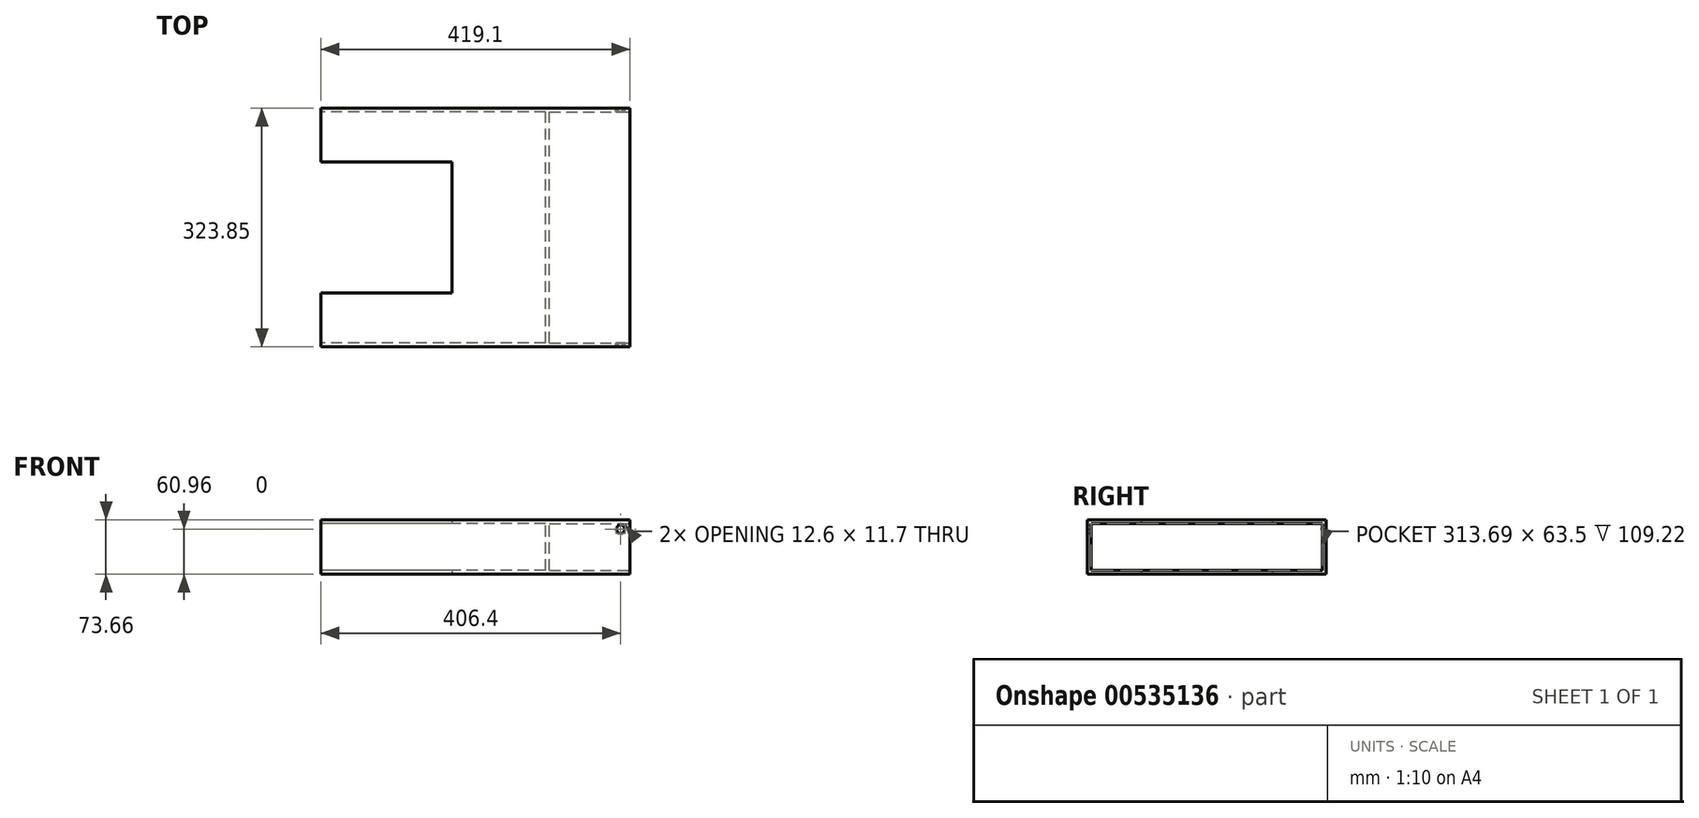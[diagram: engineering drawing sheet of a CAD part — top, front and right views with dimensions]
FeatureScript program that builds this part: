
annotation { "Feature Type Name" : "Feature", "Feature Type Description" : "" }
export const myFeature = defineFeature(function(context is Context, id is Id, definition is map)
    precondition{}
    {
        {
            var Q0;
            Q0=qCreatedBy(makeId("Front.planeOp"),FACE);
            var sketch = newSketch(context, id + "F0", { "sketchPlane" : qUnion([Q0])});
            skLineSegment(sketch, "E0.bottom", {"start": v(0, 0) * mm, "end": v(-419.1, 0) * mm});
            skLineSegment(sketch, "E0.top", {"start": v(0, 73.66) * mm, "end": v(-419.1, 73.66) * mm});
            skLineSegment(sketch, "E0.left", {"start": v(0, 0) * mm, "end": v(0, 73.66) * mm});
            skLineSegment(sketch, "E0.right", {"start": v(-419.1, 0) * mm, "end": v(-419.1, 73.66) * mm});
            skSolve(sketch);
        }
        {
            var Q0;
            Q0=makeQuery(id+"F0.imprint","IMPRINT",FACE,{"disambiguationData":[TD([[makeQuery(id+"F0.imprint","IMPRINT",EDGE,{"derivedFrom":sQuery(id+"F0.wireOp",EDGE,"E0.bottom")}),-1.0]])]});
            extrude(context, id + "F1", {"entities" : qUnion([Q0]), "depth" : 323.85 * mm, "offsetDistance" : 25.4 * mm});
        }
        {
            var Q0;
            Q0=makeQuery(id+"F1.opExtrude","SWEPT_FACE",FACE,{"disambiguationData":[OSD([sQuery(id+"F0.wireOp",EDGE,"E0.right")])]});
            var sketch = newSketch(context, id + "F2", { "sketchPlane" : qUnion([Q0])});
            skLineSegment(sketch, "E1.0", {"start": v(318.77, 68.58) * mm, "end": v(5.08, 68.58) * mm});
            skLineSegment(sketch, "E1.1", {"start": v(318.77, 5.08) * mm, "end": v(318.77, 68.58) * mm});
            skLineSegment(sketch, "E1.2", {"start": v(318.77, 5.08) * mm, "end": v(5.08, 5.08) * mm});
            skLineSegment(sketch, "E1.3", {"start": v(5.08, 5.08) * mm, "end": v(5.08, 68.58) * mm});
            skSolve(sketch);
        }
        {
            var Q0;
            Q0=qSketchRegion(id+"F2",true);
            extrude(context, id + "F3", {"entities" : qUnion([Q0]), "operationType" : NewBodyOperationType.REMOVE, "oppositeDirection" : true, "depth" : 304.8 * mm, "offsetDistance" : 25.4 * mm});
        }
        {
            var Q0;
            Q0=makeQuery(id+"F1.opExtrude","SWEPT_FACE",FACE,{"disambiguationData":[OSD([sQuery(id+"F0.wireOp",EDGE,"E0.left")])]});
            var sketch = newSketch(context, id + "F4", { "sketchPlane" : qUnion([Q0])});
            skLineSegment(sketch, "E2.0", {"start": v(-5.08, 5.08) * mm, "end": v(-5.08, 68.58) * mm});
            skLineSegment(sketch, "E2.1", {"start": v(-318.77, 5.08) * mm, "end": v(-5.08, 5.08) * mm});
            skLineSegment(sketch, "E2.2", {"start": v(-318.77, 68.58) * mm, "end": v(-318.77, 5.08) * mm});
            skLineSegment(sketch, "E2.3", {"start": v(-5.08, 68.58) * mm, "end": v(-318.77, 68.58) * mm});
            skSolve(sketch);
        }
        {
            var Q0;
            Q0=makeQuery(id+"F4.imprint","IMPRINT",FACE,{"disambiguationData":[TD([[makeQuery(id+"F4.imprint","IMPRINT",EDGE,{"derivedFrom":sQuery(id+"F4.wireOp",EDGE,"E2.0")}),1.0]])]});
            extrude(context, id + "F5", {"entities" : qUnion([Q0]), "operationType" : NewBodyOperationType.REMOVE, "oppositeDirection" : true, "depth" : 109.22 * mm, "offsetDistance" : 25.4 * mm});
        }
        {
            var Q0;
            Q0=makeQuery(id+"F0.imprint","IMPRINT",FACE,{"disambiguationData":[TD([[makeQuery(id+"F0.imprint","IMPRINT",EDGE,{"derivedFrom":sQuery(id+"F0.wireOp",EDGE,"E0.bottom")}),-1.0]])]});
            var sketch = newSketch(context, id + "F6", { "sketchPlane" : qUnion([Q0])});
            skCircle(sketch, "E3.cCircle", {"center": v(-12.7, 60.96) * mm, "radius": 6.35 * mm, "construction": true});
            skLineSegment(sketch, "E3.0", {"start": v(-16.53, 55.9) * mm, "end": v(-19, 61.75) * mm});
            skLineSegment(sketch, "E3.1", {"start": v(-19, 61.75) * mm, "end": v(-15.17, 66.81) * mm});
            skLineSegment(sketch, "E3.2", {"start": v(-15.17, 66.81) * mm, "end": v(-8.87, 66.02) * mm});
            skLineSegment(sketch, "E3.3", {"start": v(-8.87, 66.02) * mm, "end": v(-6.4, 60.17) * mm});
            skLineSegment(sketch, "E3.4", {"start": v(-6.4, 60.17) * mm, "end": v(-10.23, 55.1) * mm});
            skLineSegment(sketch, "E3.5", {"start": v(-10.23, 55.1) * mm, "end": v(-16.53, 55.9) * mm});
            skSolve(sketch);
        }
        {
            var Q0;
            Q0=qSketchRegion(id+"F6",true);
            var Q1;
            Q1=makeQuery(id+"F1.opExtrude","CAP_FACE",FACE,{"disambiguationData":[OSD([sQuery(id+"F0.wireOp",EDGE,"E0.bottom"),sQuery(id+"F0.wireOp",EDGE,"E0.top"),sQuery(id+"F0.wireOp",EDGE,"E0.left"),sQuery(id+"F0.wireOp",EDGE,"E0.right")])],"isStart":false});
            extrude(context, id + "F7", {"entities" : qUnion([Q0]), "operationType" : NewBodyOperationType.REMOVE, "endBound" : BoundingType.UP_TO_SURFACE, "depth" : 25.4 * mm, "endBoundEntityFace" : qUnion([Q1]), "offsetDistance" : 25.4 * mm});
        }
        {
            var Q0;
            Q0=makeQuery(id+"F1.opExtrude","SWEPT_FACE",FACE,{"disambiguationData":[OSD([sQuery(id+"F0.wireOp",EDGE,"E0.bottom")])]});
            var sketch = newSketch(context, id + "F8", { "sketchPlane" : qUnion([Q0])});
            skLineSegment(sketch, "E4.bottom", {"start": v(-419.1, 250.83) * mm, "end": v(-241.3, 250.83) * mm});
            skLineSegment(sketch, "E4.top", {"start": v(-419.1, 73.03) * mm, "end": v(-241.3, 73.03) * mm});
            skLineSegment(sketch, "E4.left", {"start": v(-419.1, 250.83) * mm, "end": v(-419.1, 73.03) * mm});
            skLineSegment(sketch, "E4.right", {"start": v(-241.3, 250.83) * mm, "end": v(-241.3, 73.03) * mm});
            skLineSegment(sketch, "E5", {"start": v(-419.1, 161.93) * mm, "end": v(0, 161.93) * mm, "construction": true});
            skSolve(sketch);
        }
        {
            var Q0;
            Q0=qSketchRegion(id+"F8",true);
            extrude(context, id + "F9", {"entities" : qUnion([Q0]), "operationType" : NewBodyOperationType.REMOVE, "endBound" : BoundingType.THROUGH_ALL, "oppositeDirection" : true, "depth" : 25.4 * mm, "offsetDistance" : 25.4 * mm});
        }
    });
